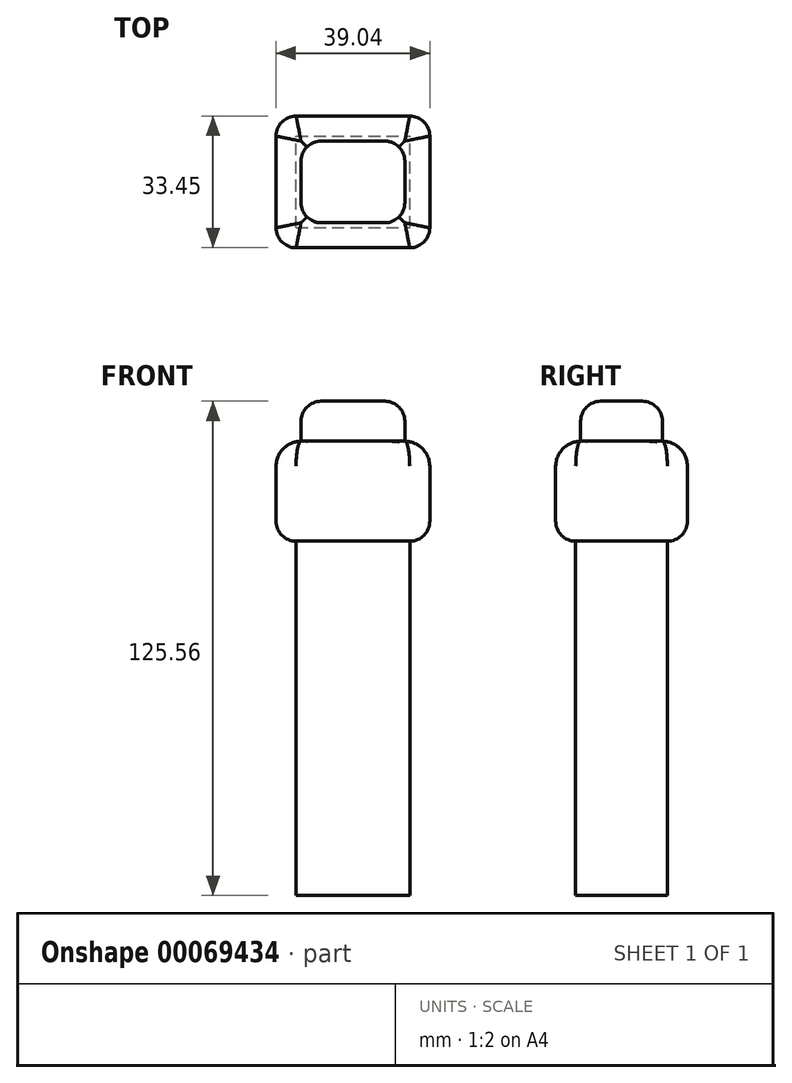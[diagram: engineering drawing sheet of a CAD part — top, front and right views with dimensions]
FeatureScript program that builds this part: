
annotation { "Feature Type Name" : "Feature", "Feature Type Description" : "" }
export const myFeature = defineFeature(function(context is Context, id is Id, definition is map)
    precondition{}
    {
        {
            var Q0;
            Q0=qCreatedBy(makeId("Top.planeOp"),FACE);
            var sketch = newSketch(context, id + "F0", { "sketchPlane" : qUnion([Q0])});
            skLineSegment(sketch, "E0.bottom", {"start": v(0, 0) * mm, "end": v(39.04, 0) * mm});
            skLineSegment(sketch, "E0.top", {"start": v(0, 33.45) * mm, "end": v(39.04, 33.45) * mm});
            skLineSegment(sketch, "E0.left", {"start": v(0, 0) * mm, "end": v(0, 33.45) * mm});
            skLineSegment(sketch, "E0.right", {"start": v(39.04, 0) * mm, "end": v(39.04, 33.45) * mm});
            skSolve(sketch);
        }
        {
            var Q0;
            Q0=makeQuery(id+"F0.imprint","IMPRINT",FACE,{"disambiguationData":[TD([[makeQuery(id+"F0.imprint","IMPRINT",EDGE,{"derivedFrom":sQuery(id+"F0.wireOp",EDGE,"E0.bottom")}),1.0]])]});
            extrude(context, id + "F1", {"entities" : qUnion([Q0]), "depth" : 25.4 * mm});
        }
        {
            var Q0;
            Q0=makeQuery(id+"F1.opExtrude","CAP_EDGE",EDGE,{"disambiguationData":[OSD([sQuery(id+"F0.wireOp",EDGE,"E0.right")])],"isStart":false});
            var Q1;
            Q1=makeQuery(id+"F1.opExtrude","CAP_EDGE",EDGE,{"disambiguationData":[OSD([sQuery(id+"F0.wireOp",EDGE,"E0.bottom")])],"isStart":false});
            var Q2;
            Q2=makeQuery(id+"F1.opExtrude","CAP_EDGE",EDGE,{"disambiguationData":[OSD([sQuery(id+"F0.wireOp",EDGE,"E0.left")])],"isStart":false});
            var Q3;
            Q3=makeQuery(id+"F1.opExtrude","CAP_EDGE",EDGE,{"disambiguationData":[OSD([sQuery(id+"F0.wireOp",EDGE,"E0.top")])],"isStart":false});
            fillet(context, id + "F2", {"entities" : qUnion([Q0, Q1, Q2, Q3]), "radius" : 6.35 * mm, "tangentPropagation" : true, "allowEdgeOverflow" : false});
        }
        {
            var Q0;
            Q0=makeQuery(id+"F2.opFillet","BLEND_EDGE",EDGE,{"blendedFrom":[makeQuery(id+"F1.opExtrude","CAP_EDGE",EDGE,{"disambiguationData":[OSD([sQuery(id+"F0.wireOp",EDGE,"E0.bottom")])],"isStart":false}),makeQuery(id+"F1.opExtrude","CAP_EDGE",EDGE,{"disambiguationData":[OSD([sQuery(id+"F0.wireOp",EDGE,"E0.right")])],"isStart":false})],"blendedInto":[]});
            var Q1;
            Q1=makeQuery(id+"F2.opFillet","BLEND_EDGE",EDGE,{"blendedFrom":[makeQuery(id+"F1.opExtrude","CAP_EDGE",EDGE,{"disambiguationData":[OSD([sQuery(id+"F0.wireOp",EDGE,"E0.top")])],"isStart":false}),makeQuery(id+"F1.opExtrude","CAP_EDGE",EDGE,{"disambiguationData":[OSD([sQuery(id+"F0.wireOp",EDGE,"E0.right")])],"isStart":false})],"blendedInto":[]});
            var Q2;
            Q2=makeQuery(id+"F2.opFillet","BLEND_EDGE",EDGE,{"blendedFrom":[makeQuery(id+"F1.opExtrude","CAP_EDGE",EDGE,{"disambiguationData":[OSD([sQuery(id+"F0.wireOp",EDGE,"E0.bottom")])],"isStart":false}),makeQuery(id+"F1.opExtrude","CAP_EDGE",EDGE,{"disambiguationData":[OSD([sQuery(id+"F0.wireOp",EDGE,"E0.left")])],"isStart":false})],"blendedInto":[]});
            var Q3;
            Q3=makeQuery(id+"F2.opFillet","BLEND_EDGE",EDGE,{"blendedFrom":[makeQuery(id+"F1.opExtrude","CAP_EDGE",EDGE,{"disambiguationData":[OSD([sQuery(id+"F0.wireOp",EDGE,"E0.top")])],"isStart":false}),makeQuery(id+"F1.opExtrude","CAP_EDGE",EDGE,{"disambiguationData":[OSD([sQuery(id+"F0.wireOp",EDGE,"E0.left")])],"isStart":false})],"blendedInto":[]});
            var Q4;
            Q4=makeQuery(id+"F1.opExtrude","CAP_EDGE",EDGE,{"disambiguationData":[OSD([sQuery(id+"F0.wireOp",EDGE,"E0.bottom")])],"isStart":true});
            var Q5;
            Q5=makeQuery(id+"F1.opExtrude","CAP_EDGE",EDGE,{"disambiguationData":[OSD([sQuery(id+"F0.wireOp",EDGE,"E0.right")])],"isStart":true});
            var Q6;
            Q6=makeQuery(id+"F1.opExtrude","CAP_EDGE",EDGE,{"disambiguationData":[OSD([sQuery(id+"F0.wireOp",EDGE,"E0.top")])],"isStart":true});
            var Q7;
            Q7=makeQuery(id+"F1.opExtrude","CAP_EDGE",EDGE,{"disambiguationData":[OSD([sQuery(id+"F0.wireOp",EDGE,"E0.left")])],"isStart":true});
            fillet(context, id + "F3", {"entities" : qUnion([Q0, Q1, Q2, Q3, Q4, Q5, Q6, Q7]), "radius" : 5.08 * mm, "tangentPropagation" : true, "allowEdgeOverflow" : false});
        }
        {
            var Q0;
            Q0=makeQuery(id+"F1.opExtrude","CAP_FACE",FACE,{"disambiguationData":[OSD([sQuery(id+"F0.wireOp",EDGE,"E0.bottom"),sQuery(id+"F0.wireOp",EDGE,"E0.top"),sQuery(id+"F0.wireOp",EDGE,"E0.left"),sQuery(id+"F0.wireOp",EDGE,"E0.right")])],"isStart":false});
            extrude(context, id + "F4", {"entities" : qUnion([Q0]), "operationType" : NewBodyOperationType.ADD, "depth" : 10.16 * mm});
        }
        {
            var Q0;
            Q0=makeQuery(id+"F1.opExtrude","CAP_FACE",FACE,{"disambiguationData":[OSD([sQuery(id+"F0.wireOp",EDGE,"E0.bottom"),sQuery(id+"F0.wireOp",EDGE,"E0.top"),sQuery(id+"F0.wireOp",EDGE,"E0.left"),sQuery(id+"F0.wireOp",EDGE,"E0.right")])],"isStart":true});
            extrude(context, id + "F5", {"entities" : qUnion([Q0]), "operationType" : NewBodyOperationType.ADD, "depth" : 90 * mm});
        }
        {
            var Q0;
            {var subQ0=sQuery(id+"F0.wireOp",EDGE,"E0.right");var subQ1=sQuery(id+"F0.wireOp",EDGE,"E0.left");var subQ2=sQuery(id+"F0.wireOp",EDGE,"E0.top");var subQ3=sQuery(id+"F0.wireOp",EDGE,"E0.bottom");Q0=makeQuery(id+"F4.opExtrude","CAP_EDGE",EDGE,{"disambiguationData":[OSD([subQ3,subQ2,subQ1,subQ0]),TDD([makeQuery(id+"F2.opFillet","BLEND_EDGE",EDGE,{"blendedFrom":[makeQuery(id+"F1.opExtrude","CAP_EDGE",EDGE,{"disambiguationData":[OSD([subQ0])],"isStart":false}),makeQuery(id+"F1.opExtrude","CAP_FACE",FACE,{"disambiguationData":[OSD([subQ3,subQ2,subQ1,subQ0])],"isStart":false})],"blendedInto":[makeQuery(id+"F1.opExtrude","CAP_FACE",FACE,{"disambiguationData":[OSD([subQ3,subQ2,subQ1,subQ0])],"isStart":false})]})])],"isStart":false});}
            var Q1;
            {var subQ0=sQuery(id+"F0.wireOp",EDGE,"E0.right");var subQ1=sQuery(id+"F0.wireOp",EDGE,"E0.left");var subQ2=sQuery(id+"F0.wireOp",EDGE,"E0.top");var subQ3=sQuery(id+"F0.wireOp",EDGE,"E0.bottom");Q1=makeQuery(id+"F4.opExtrude","CAP_EDGE",EDGE,{"disambiguationData":[OSD([subQ3,subQ2,subQ1,subQ0]),TDD([makeQuery(id+"F2.opFillet","BLEND_EDGE",EDGE,{"blendedFrom":[makeQuery(id+"F1.opExtrude","CAP_EDGE",EDGE,{"disambiguationData":[OSD([subQ2])],"isStart":false}),makeQuery(id+"F1.opExtrude","CAP_FACE",FACE,{"disambiguationData":[OSD([subQ3,subQ2,subQ1,subQ0])],"isStart":false})],"blendedInto":[makeQuery(id+"F1.opExtrude","CAP_FACE",FACE,{"disambiguationData":[OSD([subQ3,subQ2,subQ1,subQ0])],"isStart":false})]})])],"isStart":false});}
            var Q2;
            {var subQ0=sQuery(id+"F0.wireOp",EDGE,"E0.right");var subQ1=sQuery(id+"F0.wireOp",EDGE,"E0.left");var subQ2=sQuery(id+"F0.wireOp",EDGE,"E0.top");var subQ3=sQuery(id+"F0.wireOp",EDGE,"E0.bottom");Q2=makeQuery(id+"F4.opExtrude","CAP_EDGE",EDGE,{"disambiguationData":[OSD([subQ3,subQ2,subQ1,subQ0]),TDD([makeQuery(id+"F2.opFillet","BLEND_EDGE",EDGE,{"blendedFrom":[makeQuery(id+"F1.opExtrude","CAP_EDGE",EDGE,{"disambiguationData":[OSD([subQ1])],"isStart":false}),makeQuery(id+"F1.opExtrude","CAP_FACE",FACE,{"disambiguationData":[OSD([subQ3,subQ2,subQ1,subQ0])],"isStart":false})],"blendedInto":[makeQuery(id+"F1.opExtrude","CAP_FACE",FACE,{"disambiguationData":[OSD([subQ3,subQ2,subQ1,subQ0])],"isStart":false})]})])],"isStart":false});}
            var Q3;
            {var subQ0=sQuery(id+"F0.wireOp",EDGE,"E0.right");var subQ1=sQuery(id+"F0.wireOp",EDGE,"E0.left");var subQ2=sQuery(id+"F0.wireOp",EDGE,"E0.top");var subQ3=sQuery(id+"F0.wireOp",EDGE,"E0.bottom");Q3=makeQuery(id+"F4.opExtrude","CAP_EDGE",EDGE,{"disambiguationData":[OSD([subQ3,subQ2,subQ1,subQ0]),TDD([makeQuery(id+"F2.opFillet","BLEND_EDGE",EDGE,{"blendedFrom":[makeQuery(id+"F1.opExtrude","CAP_EDGE",EDGE,{"disambiguationData":[OSD([subQ3])],"isStart":false}),makeQuery(id+"F1.opExtrude","CAP_FACE",FACE,{"disambiguationData":[OSD([subQ3,subQ2,subQ1,subQ0])],"isStart":false})],"blendedInto":[makeQuery(id+"F1.opExtrude","CAP_FACE",FACE,{"disambiguationData":[OSD([subQ3,subQ2,subQ1,subQ0])],"isStart":false})]})])],"isStart":false});}
            var Q4;
            {var subQ0=sQuery(id+"F0.wireOp",EDGE,"E0.right");var subQ1=sQuery(id+"F0.wireOp",EDGE,"E0.left");var subQ2=sQuery(id+"F0.wireOp",EDGE,"E0.top");var subQ3=sQuery(id+"F0.wireOp",EDGE,"E0.bottom");Q4=makeQuery(id+"F4.opExtrude","SWEPT_EDGE",EDGE,{"disambiguationData":[OSD([subQ3,subQ2,subQ1,subQ0]),TDD([makeQuery(id+"F3.opFillet","BLEND_VERTEX",VERTEX,{"blendedFrom":[makeQuery(id+"F2.opFillet","BLEND_EDGE",EDGE,{"blendedFrom":[makeQuery(id+"F1.opExtrude","CAP_EDGE",EDGE,{"disambiguationData":[OSD([subQ3])],"isStart":false}),makeQuery(id+"F1.opExtrude","CAP_EDGE",EDGE,{"disambiguationData":[OSD([subQ0])],"isStart":false})],"blendedInto":[]}),makeQuery(id+"F2.opFillet","BLEND_FACE",FACE,{"disambiguationData":[OSD([subQ3])]}),makeQuery(id+"F2.opFillet","BLEND_FACE",FACE,{"disambiguationData":[OSD([subQ0])]}),makeQuery(id+"F1.opExtrude","CAP_FACE",FACE,{"disambiguationData":[OSD([subQ3,subQ2,subQ1,subQ0])],"isStart":false})],"blendedInto":[makeQuery(id+"F2.opFillet","BLEND_FACE",FACE,{"disambiguationData":[OSD([subQ3])]}),makeQuery(id+"F2.opFillet","BLEND_FACE",FACE,{"disambiguationData":[OSD([subQ0])]}),makeQuery(id+"F1.opExtrude","CAP_FACE",FACE,{"disambiguationData":[OSD([subQ3,subQ2,subQ1,subQ0])],"isStart":false})]})])]});}
            var Q5;
            {var subQ0=sQuery(id+"F0.wireOp",EDGE,"E0.right");var subQ1=sQuery(id+"F0.wireOp",EDGE,"E0.left");var subQ2=sQuery(id+"F0.wireOp",EDGE,"E0.top");var subQ3=sQuery(id+"F0.wireOp",EDGE,"E0.bottom");Q5=makeQuery(id+"F4.opExtrude","SWEPT_EDGE",EDGE,{"disambiguationData":[OSD([subQ3,subQ2,subQ1,subQ0]),TDD([makeQuery(id+"F3.opFillet","BLEND_VERTEX",VERTEX,{"blendedFrom":[makeQuery(id+"F2.opFillet","BLEND_EDGE",EDGE,{"blendedFrom":[makeQuery(id+"F1.opExtrude","CAP_EDGE",EDGE,{"disambiguationData":[OSD([subQ2])],"isStart":false}),makeQuery(id+"F1.opExtrude","CAP_EDGE",EDGE,{"disambiguationData":[OSD([subQ1])],"isStart":false})],"blendedInto":[]}),makeQuery(id+"F2.opFillet","BLEND_FACE",FACE,{"disambiguationData":[OSD([subQ2])]}),makeQuery(id+"F2.opFillet","BLEND_FACE",FACE,{"disambiguationData":[OSD([subQ1])]}),makeQuery(id+"F1.opExtrude","CAP_FACE",FACE,{"disambiguationData":[OSD([subQ3,subQ2,subQ1,subQ0])],"isStart":false})],"blendedInto":[makeQuery(id+"F2.opFillet","BLEND_FACE",FACE,{"disambiguationData":[OSD([subQ2])]}),makeQuery(id+"F2.opFillet","BLEND_FACE",FACE,{"disambiguationData":[OSD([subQ1])]}),makeQuery(id+"F1.opExtrude","CAP_FACE",FACE,{"disambiguationData":[OSD([subQ3,subQ2,subQ1,subQ0])],"isStart":false})]})])]});}
            var Q6;
            {var subQ0=sQuery(id+"F0.wireOp",EDGE,"E0.right");var subQ1=sQuery(id+"F0.wireOp",EDGE,"E0.left");var subQ2=sQuery(id+"F0.wireOp",EDGE,"E0.top");var subQ3=sQuery(id+"F0.wireOp",EDGE,"E0.bottom");Q6=makeQuery(id+"F4.opExtrude","SWEPT_EDGE",EDGE,{"disambiguationData":[OSD([subQ3,subQ2,subQ1,subQ0]),TDD([makeQuery(id+"F3.opFillet","BLEND_VERTEX",VERTEX,{"blendedFrom":[makeQuery(id+"F2.opFillet","BLEND_EDGE",EDGE,{"blendedFrom":[makeQuery(id+"F1.opExtrude","CAP_EDGE",EDGE,{"disambiguationData":[OSD([subQ2])],"isStart":false}),makeQuery(id+"F1.opExtrude","CAP_EDGE",EDGE,{"disambiguationData":[OSD([subQ0])],"isStart":false})],"blendedInto":[]}),makeQuery(id+"F2.opFillet","BLEND_FACE",FACE,{"disambiguationData":[OSD([subQ2])]}),makeQuery(id+"F2.opFillet","BLEND_FACE",FACE,{"disambiguationData":[OSD([subQ0])]}),makeQuery(id+"F1.opExtrude","CAP_FACE",FACE,{"disambiguationData":[OSD([subQ3,subQ2,subQ1,subQ0])],"isStart":false})],"blendedInto":[makeQuery(id+"F2.opFillet","BLEND_FACE",FACE,{"disambiguationData":[OSD([subQ2])]}),makeQuery(id+"F2.opFillet","BLEND_FACE",FACE,{"disambiguationData":[OSD([subQ0])]}),makeQuery(id+"F1.opExtrude","CAP_FACE",FACE,{"disambiguationData":[OSD([subQ3,subQ2,subQ1,subQ0])],"isStart":false})]})])]});}
            var Q7;
            {var subQ0=sQuery(id+"F0.wireOp",EDGE,"E0.right");var subQ1=sQuery(id+"F0.wireOp",EDGE,"E0.left");var subQ2=sQuery(id+"F0.wireOp",EDGE,"E0.top");var subQ3=sQuery(id+"F0.wireOp",EDGE,"E0.bottom");Q7=makeQuery(id+"F4.opExtrude","SWEPT_EDGE",EDGE,{"disambiguationData":[OSD([subQ3,subQ2,subQ1,subQ0]),TDD([makeQuery(id+"F3.opFillet","BLEND_VERTEX",VERTEX,{"blendedFrom":[makeQuery(id+"F2.opFillet","BLEND_EDGE",EDGE,{"blendedFrom":[makeQuery(id+"F1.opExtrude","CAP_EDGE",EDGE,{"disambiguationData":[OSD([subQ3])],"isStart":false}),makeQuery(id+"F1.opExtrude","CAP_EDGE",EDGE,{"disambiguationData":[OSD([subQ1])],"isStart":false})],"blendedInto":[]}),makeQuery(id+"F2.opFillet","BLEND_FACE",FACE,{"disambiguationData":[OSD([subQ3])]}),makeQuery(id+"F2.opFillet","BLEND_FACE",FACE,{"disambiguationData":[OSD([subQ1])]}),makeQuery(id+"F1.opExtrude","CAP_FACE",FACE,{"disambiguationData":[OSD([subQ3,subQ2,subQ1,subQ0])],"isStart":false})],"blendedInto":[makeQuery(id+"F2.opFillet","BLEND_FACE",FACE,{"disambiguationData":[OSD([subQ3])]}),makeQuery(id+"F2.opFillet","BLEND_FACE",FACE,{"disambiguationData":[OSD([subQ1])]}),makeQuery(id+"F1.opExtrude","CAP_FACE",FACE,{"disambiguationData":[OSD([subQ3,subQ2,subQ1,subQ0])],"isStart":false})]})])]});}
            fillet(context, id + "F6", {"entities" : qUnion([Q0, Q1, Q2, Q3, Q4, Q5, Q6, Q7]), "radius" : 5.08 * mm, "tangentPropagation" : true, "allowEdgeOverflow" : false});
        }
    });
